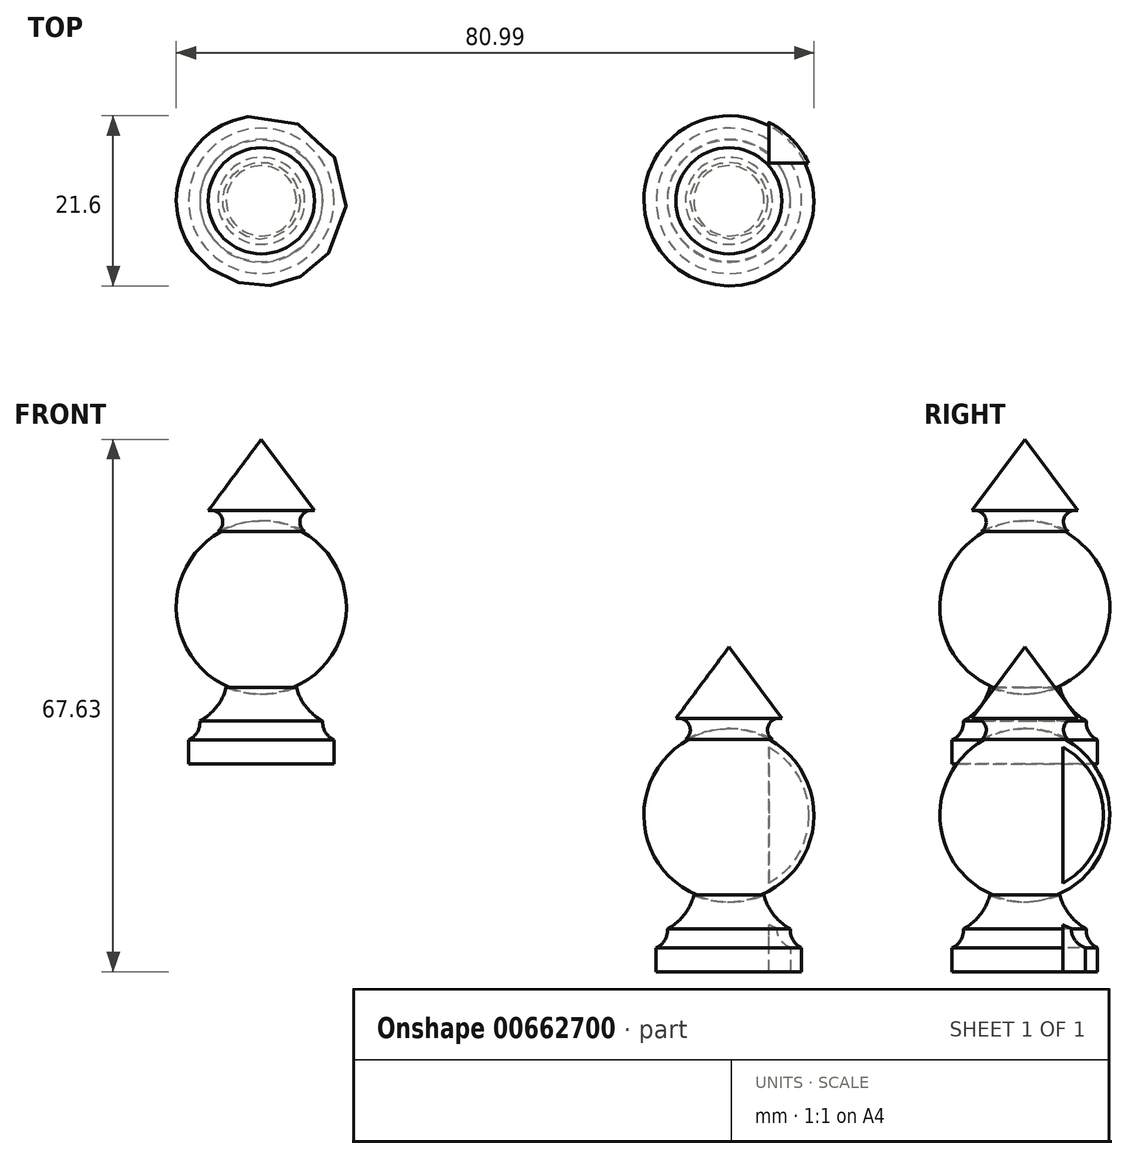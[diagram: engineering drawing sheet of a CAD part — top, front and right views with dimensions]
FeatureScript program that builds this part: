
annotation { "Feature Type Name" : "Feature", "Feature Type Description" : "" }
export const myFeature = defineFeature(function(context is Context, id is Id, definition is map)
    precondition{}
    {
        {
            var Q0;
            Q0=qCreatedBy(makeId("Front.planeOp"),FACE);
            var sketch = newSketch(context, id + "F0", { "sketchPlane" : qUnion([Q0])});
            skArc(sketch, "E0", {"start": v(-59.2, 40.8) * mm, "mid": v(-64.85, 30.59) * mm, "end": v(-58.13, 21.04) * mm});
            skLineSegment(sketch, "E1", {"start": v(-53.67, 52.53) * mm, "end": v(-53.67, 11.3) * mm});
            skLineSegment(sketch, "E2", {"start": v(-53.67, 11.3) * mm, "end": v(-62.9, 11.3) * mm});
            skLineSegment(sketch, "E3", {"start": v(-62.9, 11.3) * mm, "end": v(-62.9, 14.33) * mm});
            skArc(sketch, "E4", {"start": v(-61.48, 16.77) * mm, "mid": v(-59.35, 18.55) * mm, "end": v(-58.13, 21.04) * mm});
            skArc(sketch, "E5", {"start": v(-59.2, 40.8) * mm, "mid": v(-58.7, 42.64) * mm, "end": v(-60.41, 43.47) * mm});
            skArc(sketch, "E6", {"start": v(-62.9, 14.33) * mm, "mid": v(-61.81, 15.32) * mm, "end": v(-61.48, 16.77) * mm});
            skLineSegment(sketch, "E7", {"start": v(-60.41, 43.47) * mm, "end": v(-53.67, 52.53) * mm});
            skSolve(sketch);
        }
        {
            var Q0;
            Q0=qSketchRegion(id+"F0",true);
            var Q1;
            Q1=sQuery(id+"F0.wireOp",EDGE,"E1");
            revolve(context, id + "F1", {"entities" : qUnion([Q0]), "axis" : qUnion([Q1]), "revolveType" : RevolveType.FULL});
        }
        {
            var Q0;
            Q0=qCreatedBy(makeId("Front.planeOp"),FACE);
            var sketch = newSketch(context, id + "F2", { "sketchPlane" : qUnion([Q0])});
            skArc(sketch, "E8", {"start": v(0.2, 14.4) * mm, "mid": v(-5.46, 4.18) * mm, "end": v(1.27, -5.37) * mm});
            skLineSegment(sketch, "E9", {"start": v(5.72, 26.12) * mm, "end": v(5.72, -15.1) * mm});
            skLineSegment(sketch, "E10", {"start": v(5.72, -15.1) * mm, "end": v(-3.51, -15.1) * mm});
            skLineSegment(sketch, "E11", {"start": v(-3.51, -15.1) * mm, "end": v(-3.51, -12.08) * mm});
            skArc(sketch, "E12", {"start": v(-2.09, -9.64) * mm, "mid": v(0.05, -7.86) * mm, "end": v(1.27, -5.37) * mm});
            skArc(sketch, "E13", {"start": v(0.2, 14.4) * mm, "mid": v(0.69, 16.23) * mm, "end": v(-1.02, 17.06) * mm});
            skArc(sketch, "E14", {"start": v(-3.51, -12.08) * mm, "mid": v(-2.42, -11.09) * mm, "end": v(-2.09, -9.64) * mm});
            skLineSegment(sketch, "E15", {"start": v(-1.02, 17.06) * mm, "end": v(5.72, 26.12) * mm});
            skSolve(sketch);
        }
        {
            var Q0;
            Q0=makeQuery(id+"F2.imprint","IMPRINT",FACE,{"disambiguationData":[TD([[makeQuery(id+"F2.imprint","IMPRINT",EDGE,{"derivedFrom":sQuery(id+"F2.wireOp",EDGE,"E8")}),1.0]])]});
            var Q1;
            Q1=sQuery(id+"F2.wireOp",EDGE,"E8");
            var Q2;
            Q2=sQuery(id+"F2.wireOp",EDGE,"E9");
            var Q3;
            Q3=sQuery(id+"F2.wireOp",EDGE,"E10");
            var Q4;
            Q4=sQuery(id+"F2.wireOp",EDGE,"E11");
            var Q5;
            Q5=sQuery(id+"F2.wireOp",EDGE,"E12");
            var Q6;
            Q6=sQuery(id+"F2.wireOp",EDGE,"E13");
            var Q7;
            Q7=sQuery(id+"F2.wireOp",EDGE,"E14");
            var Q8;
            Q8=sQuery(id+"F2.wireOp",EDGE,"E15");
            var Q9;
            Q9=sQuery(id+"F2.wireOp",EDGE,"E9");
            revolve(context, id + "F3", {"entities" : qUnion([Q0]), "surfaceEntities" : qUnion([Q1, Q2, Q3, Q4, Q5, Q6, Q7, Q8]), "axis" : qUnion([Q9]), "revolveType" : RevolveType.FULL});
        }
        {
            var Q0;
            Q0=qCreatedBy(makeId("Top.planeOp"),FACE);
            var sketch = newSketch(context, id + "F4", { "sketchPlane" : qUnion([Q0])});
            skLineSegment(sketch, "E16", {"start": v(11.45, 11.28) * mm, "end": v(16.97, 11.28) * mm});
            skLineSegment(sketch, "E17", {"start": v(16.97, 11.28) * mm, "end": v(16.97, 5.64) * mm});
            skPoint(sketch, "E18.startSnap0", {"position": v(16.97, 5.64) * mm});
            skPoint(sketch, "E18.startSnap1", {"position": v(11.45, 11.28) * mm});
            skPoint(sketch, "E19.end.orphan", {"position": v(5.94, 11.28) * mm});
            skPoint(sketch, "E20.start.orphan", {"position": v(16.97, 0) * mm});
            skLineSegment(sketch, "E21", {"start": v(10.8, 4.8) * mm, "end": v(16.97, 4.8) * mm});
            skLineSegment(sketch, "E22", {"start": v(16.97, 4.8) * mm, "end": v(16.97, 5.64) * mm});
            skLineSegment(sketch, "E23", {"start": v(10.8, 4.8) * mm, "end": v(10.8, 11.28) * mm});
            skLineSegment(sketch, "E24", {"start": v(10.8, 11.28) * mm, "end": v(11.45, 11.28) * mm});
            skPoint(sketch, "E18.start.orphan", {"position": v(11.45, 5.64) * mm});
            skSolve(sketch);
        }
        {
            var Q0;
            Q0=makeQuery(id+"F4.imprint","IMPRINT",FACE,{"disambiguationData":[TD([[makeQuery(id+"F4.imprint","IMPRINT",EDGE,{"derivedFrom":sQuery(id+"F4.wireOp",EDGE,"E16")}),-1.0]])]});
            extrude(context, id + "F5", {"entities" : qUnion([Q0]), "operationType" : NewBodyOperationType.REMOVE, "oppositeDirection" : true, "depth" : 25 * mm, "offsetDistance" : 25 * mm, "hasSecondDirection" : true, "secondDirectionOppositeDirection" : false, "secondDirectionDepth" : 25 * mm});
        }
    });
